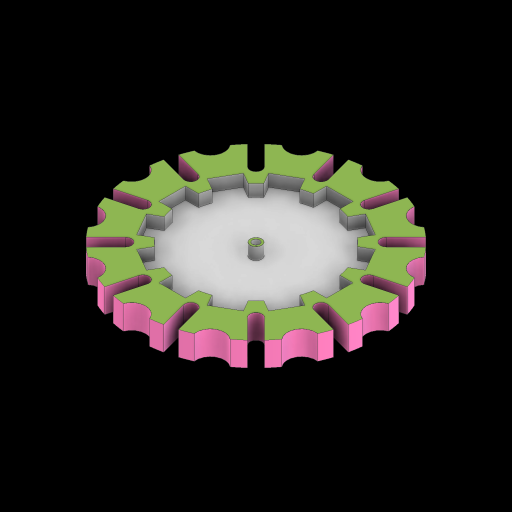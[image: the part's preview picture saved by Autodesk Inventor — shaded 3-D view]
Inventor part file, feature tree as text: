
AUTODESK INVENTOR PART (.ipt)
format: ipt  version: 2023 (Build 270158000, 158)  size: 501,248 bytes
history: native  units: mm
features: sketch x5, extrude x3
ambient origin geometry x8: Origin, YZ Plane, XZ Plane, XY Plane, X Axis, Y Axis, Z Axis, Center Point
bodies: Solid1 (feature_tree)
feature tree (8):
  sketch  "Sketch1"  dims[d1=80.0mm d2=100.0mm d3=22.5deg d4=20.712mm d5=50.0mm d6=54.123064mm d7=10.0mm d8=25.858174mm d9=65.0mm d10=360.0deg d11=7.0mm d12=7.0mm d13=15.0mm d14=15.0mm d15=10.0mm d16=200.0mm]
  extrude  "Extrusion1"  Depth=10.0mm
  sketch  "Sketch3"  dims[d20=10.0mm d21=10.0mm]
  extrude  "Extrusion4"  TaperAngle=90.0deg  [1 undecoded]
  extrude  "Extrusion5"  Depth=10.0mm
  sketch  "Sketch2"  dims[d17=15.0deg d19=90.0deg]
  sketch  "Sketch4"  dims[d22=80.0mm]
  sketch  "Sketch5"  dims[d23=120.0mm d25=360.0deg d27=6.0mm d28=5.0mm d29=20.0mm d30=0.0mm d34=120.0mm d36=360.0deg d41=120.0mm d42=124.403mm d48=360.0deg d52=120.0mm d54=120.0mm d55=360.0deg d56=360.0deg d57=10.0mm d58=0.0mm d59=10.0mm d60=9.5mm d61=10.0mm d62=0.0mm]
note: 1 required parameter value undecoded (feature->parameter linkage not recoverable at this tier; creation-order binding heuristic only, values carry confidence <= 0.55)
